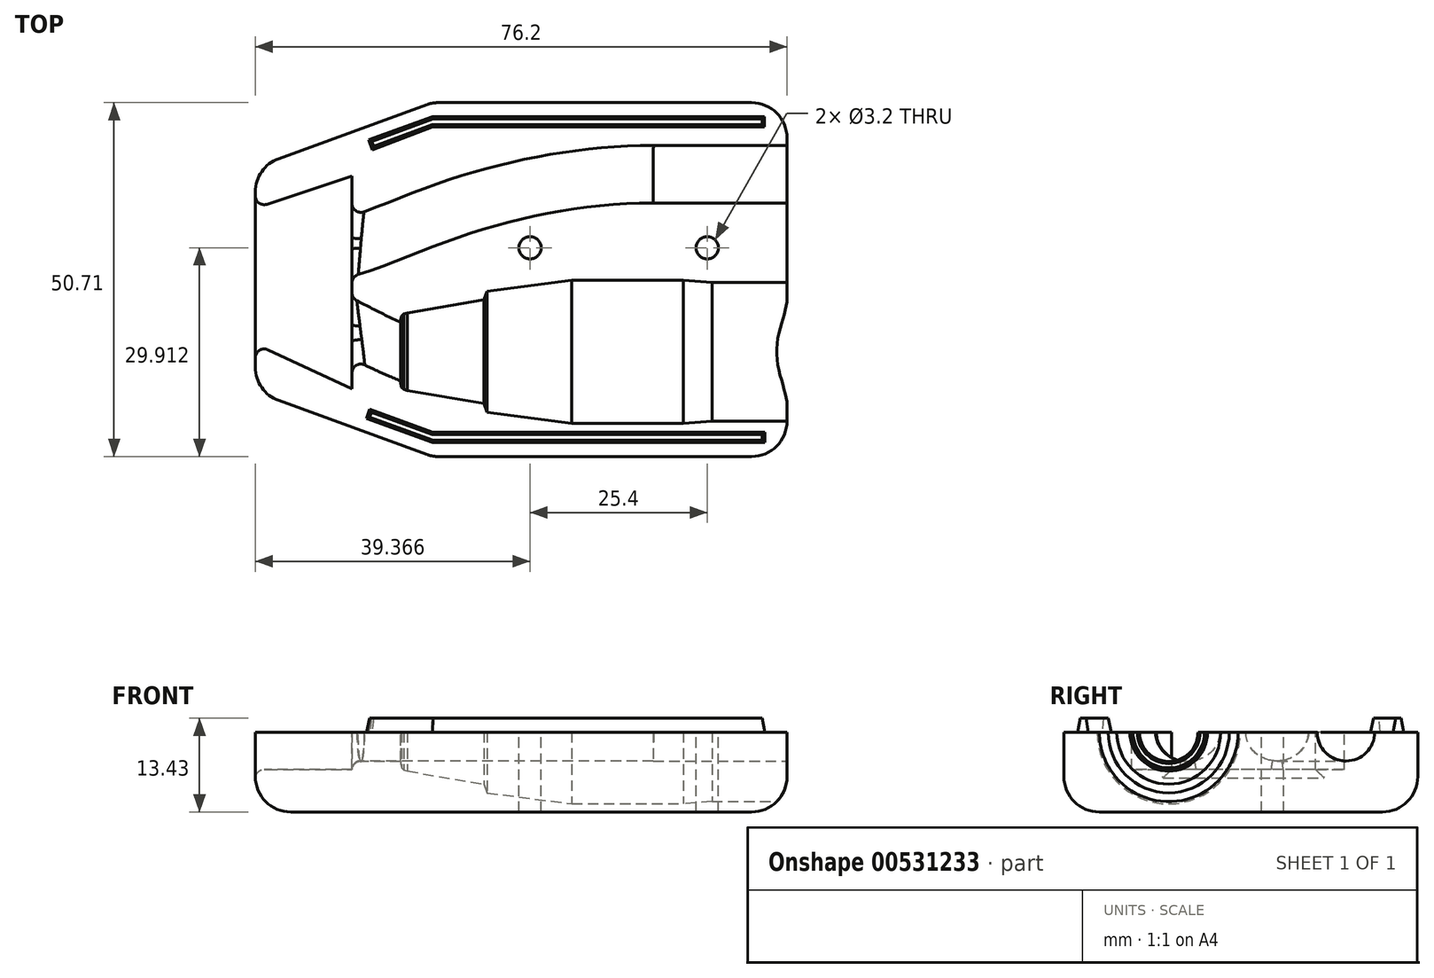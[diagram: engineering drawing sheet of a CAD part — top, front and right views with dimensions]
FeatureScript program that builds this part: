
annotation { "Feature Type Name" : "Feature", "Feature Type Description" : "" }
export const myFeature = defineFeature(function(context is Context, id is Id, definition is map)
    precondition{}
    {
        {
            var Q0;
            Q0=qCreatedBy(makeId("Top.planeOp"),FACE);
            var sketch = newSketch(context, id + "F0", { "sketchPlane" : qUnion([Q0])});
            skLineSegment(sketch, "E0", {"start": v(-28.61, 2.44) * mm, "end": v(45.8, 2.44) * mm});
            skLineSegment(sketch, "E1", {"start": v(45.8, 2.44) * mm, "end": v(45.8, -7.5) * mm});
            skLineSegment(sketch, "E2", {"start": v(45.8, -7.5) * mm, "end": v(33.92, -7.5) * mm});
            skLineSegment(sketch, "E3", {"start": v(33.92, -7.5) * mm, "end": v(31.07, -7.5) * mm});
            skLineSegment(sketch, "E4", {"start": v(31.07, -7.5) * mm, "end": v(15.98, -7.5) * mm});
            skLineSegment(sketch, "E5", {"start": v(15.98, -7.5) * mm, "end": v(11.85, -7.82) * mm});
            skLineSegment(sketch, "E6", {"start": v(11.85, -7.82) * mm, "end": v(-4.1, -7.82) * mm});
            skLineSegment(sketch, "E7", {"start": v(-4.1, -7.82) * mm, "end": v(-16.21, -6.24) * mm});
            skLineSegment(sketch, "E8", {"start": v(-16.21, -6.24) * mm, "end": v(-16.67, -5) * mm});
            skLineSegment(sketch, "E9", {"start": v(-16.67, -5) * mm, "end": v(-27.65, -3.12) * mm});
            skLineSegment(sketch, "E10", {"start": v(-27.65, -3.12) * mm, "end": v(-28.19, -2.96) * mm});
            skLineSegment(sketch, "E11", {"start": v(-28.19, -2.96) * mm, "end": v(-28.49, -2.68) * mm});
            skLineSegment(sketch, "E12", {"start": v(-28.49, -2.68) * mm, "end": v(-28.63, -2.06) * mm});
            skLineSegment(sketch, "E13", {"start": v(-28.63, -2.06) * mm, "end": v(-28.61, 2.44) * mm});
            skLineSegment(sketch, "E14.top", {"start": v(32.8, 22.64) * mm, "end": v(45.8, 22.64) * mm});
            skLineSegment(sketch, "E14.right", {"start": v(45.8, 27.84) * mm, "end": v(45.8, 22.64) * mm});
            skLineSegment(sketch, "E15", {"start": v(32.8, 23.72) * mm, "end": v(24.8, 23.72) * mm});
            skLineSegment(sketch, "E16", {"start": v(24.8, 23.72) * mm, "end": v(24.8, 27.84) * mm});
            skLineSegment(sketch, "E17", {"start": v(45.8, 27.84) * mm, "end": v(24.8, 27.84) * mm});
            skLineSegment(sketch, "E18", {"start": v(32.8, 22.64) * mm, "end": v(32.8, 23.72) * mm});
            skLineSegment(sketch, "E19.MirrorCS", {"start": v(32.8, 33.05) * mm, "end": v(32.8, 31.97) * mm});
            skLineSegment(sketch, "E20.MirrorCS", {"start": v(32.8, 33.05) * mm, "end": v(45.8, 33.05) * mm});
            skLineSegment(sketch, "E21.MirrorCS", {"start": v(45.8, 27.84) * mm, "end": v(45.8, 33.05) * mm});
            skLineSegment(sketch, "E22.MirrorCS", {"start": v(24.8, 31.97) * mm, "end": v(24.8, 27.84) * mm});
            skLineSegment(sketch, "E23.MirrorCS", {"start": v(32.8, 31.97) * mm, "end": v(24.8, 31.97) * mm});
            skLineSegment(sketch, "E24.MirrorCS", {"start": v(-28.19, 7.85) * mm, "end": v(-28.49, 7.56) * mm});
            skLineSegment(sketch, "E25.MirrorCS", {"start": v(-28.49, 7.56) * mm, "end": v(-28.63, 6.94) * mm});
            skLineSegment(sketch, "E26.MirrorCS", {"start": v(33.92, 12.39) * mm, "end": v(31.07, 12.39) * mm});
            skLineSegment(sketch, "E27.MirrorCS", {"start": v(-27.65, 8) * mm, "end": v(-28.19, 7.85) * mm});
            skLineSegment(sketch, "E28.MirrorCS", {"start": v(-16.21, 11.12) * mm, "end": v(-16.67, 9.89) * mm});
            skLineSegment(sketch, "E29.MirrorCS", {"start": v(-16.67, 9.89) * mm, "end": v(-27.65, 8) * mm});
            skLineSegment(sketch, "E30.MirrorCS", {"start": v(11.85, 12.7) * mm, "end": v(-4.1, 12.7) * mm});
            skLineSegment(sketch, "E31.MirrorCS", {"start": v(45.8, 12.39) * mm, "end": v(33.92, 12.39) * mm});
            skLineSegment(sketch, "E32.MirrorCS", {"start": v(-4.1, 12.7) * mm, "end": v(-16.21, 11.12) * mm});
            skLineSegment(sketch, "E33.MirrorCS", {"start": v(15.98, 12.39) * mm, "end": v(11.85, 12.7) * mm});
            skLineSegment(sketch, "E34.MirrorCS", {"start": v(31.07, 12.39) * mm, "end": v(15.98, 12.39) * mm});
            skLineSegment(sketch, "E35.MirrorCS", {"start": v(45.8, 2.44) * mm, "end": v(45.8, 12.39) * mm});
            skLineSegment(sketch, "E36.MirrorCS", {"start": v(-28.63, 6.94) * mm, "end": v(-28.61, 2.44) * mm});
            skSolve(sketch);
        }
        {
            var Q0;
            Q0=qCreatedBy(makeId("Top.planeOp"),FACE);
            var sketch = newSketch(context, id + "F1", { "sketchPlane" : qUnion([Q0])});
            skLineSegment(sketch, "E37.0", {"start": v(45.8, 2.44) * mm, "end": v(45.8, -7.5) * mm});
            skLineSegment(sketch, "E38.0", {"start": v(45.8, 27.84) * mm, "end": v(45.8, 22.64) * mm});
            skLineSegment(sketch, "E39", {"start": v(26.75, 38.13) * mm, "end": v(26.75, -12.58) * mm});
            skLineSegment(sketch, "E40", {"start": v(26.75, -12.58) * mm, "end": v(-24.05, -12.58) * mm});
            skLineSegment(sketch, "E41", {"start": v(-24.05, -12.58) * mm, "end": v(-49.45, -3.34) * mm});
            skLineSegment(sketch, "E42", {"start": v(-49.45, -3.34) * mm, "end": v(-49.45, 28.88) * mm});
            skLineSegment(sketch, "E43", {"start": v(-49.45, 28.88) * mm, "end": v(-24.05, 38.13) * mm});
            skLineSegment(sketch, "E44", {"start": v(-24.05, 38.13) * mm, "end": v(26.75, 38.13) * mm});
            skLineSegment(sketch, "E45.0", {"start": v(45.8, 27.84) * mm, "end": v(45.8, 33.05) * mm});
            skSolve(sketch);
        }
        {
            var Q0;
            Q0 = qSketchRegion(id + "F1", true);
            extrude(context, id + "F2", {"entities" : qUnion([Q0]), "oppositeDirection" : true, "depth" : 11.43 * mm, "offsetDistance" : 25.4 * mm});
        }
        {
            var Q0;
            Q0=makeQuery(id+"F0.imprint","IMPRINT",FACE,{"disambiguationData":[TD([[makeQuery(id+"F0.imprint","IMPRINT",EDGE,{"derivedFrom":sQuery(id+"F0.wireOp",EDGE,"E0")}),-1.0]])]});
            var Q1;
            Q1=sQuery(id+"F0.wireOp",EDGE,"E0");
            revolve(context, id + "F3", {"operationType" : NewBodyOperationType.REMOVE, "entities" : qUnion([Q0]), "axis" : qUnion([Q1]), "revolveType" : RevolveType.FULL, "oppositeDirection" : true});
        }
        {
            var Q0;
            Q0=makeQuery(id+"F0.imprint","IMPRINT",FACE,{"disambiguationData":[TD([[makeQuery(id+"F0.imprint","IMPRINT",EDGE,{"derivedFrom":sQuery(id+"F0.wireOp",EDGE,"E14.top")}),1.0]])]});
            var Q1;
            Q1=sQuery(id+"F0.wireOp",EDGE,"E17");
            revolve(context, id + "F4", {"operationType" : NewBodyOperationType.REMOVE, "entities" : qUnion([Q0]), "axis" : qUnion([Q1]), "revolveType" : RevolveType.FULL});
        }
        {
            var Q0;
            Q0=makeQuery(id+"F2.opExtrude","CAP_FACE",FACE,{"disambiguationData":[OSD([sQuery(id+"F1.wireOp",EDGE,"FN9DgEXL-DUnT-EqR8-ggIH-wTex11pTKOJ6"),sQuery(id+"F1.wireOp",EDGE,"Mmaicck8-LA38-ALDy-QV3c-pMFCgAv4KP83"),sQuery(id+"F1.wireOp",EDGE,"E39"),sQuery(id+"F1.wireOp",EDGE,"E40"),sQuery(id+"F1.wireOp",EDGE,"E41"),sQuery(id+"F1.wireOp",EDGE,"E42"),sQuery(id+"F1.wireOp",EDGE,"E43"),sQuery(id+"F1.wireOp",EDGE,"E44")])],"isStart":true});
            var sketch = newSketch(context, id + "F5", { "sketchPlane" : qUnion([Q0])});
            skLineSegment(sketch, "E46.0", {"start": v(-28.61, 2.44) * mm, "end": v(45.8, 2.44) * mm});
            skFitSpline(sketch, "E47", {"points": [v(-28.61, 2.44) * mm, v(-48.07, 10.49) * mm, v(-83.77, 9.93) * mm], "startDerivative": vector(-48.46, 20.5) * mm, "endDerivative": vector(-77.25, 2.74) * mm});
            skSolve(sketch);
        }
        {
            var Q0;
            Q0=sQuery(id+"F5.wireOp",VERTEX,"E47.0.internal");
            var Q1;
            Q1=sQuery(id+"F5.wireOp",EDGE,"E46.0");
            cPlane(context, id + "F6", {"entities" : qUnion([Q0, Q1]), "cplaneType" : CPlaneType.LINE_POINT, "offset" : 25.4 * mm, "width" : 152.4 * mm, "height" : 152.4 * mm});
        }
        {
            var Q0;
            Q0=qCreatedBy(id+"F6.planeOp",FACE);
            var sketch = newSketch(context, id + "F7", { "sketchPlane" : qUnion([Q0])});
            skCircle(sketch, "E48", {"center": v(2.44, 0) * mm, "radius": 4.2 * mm});
            skSolve(sketch);
        }
        {
            var Q0;
            Q0 = qSketchRegion(id + "F7", true);
            var Q1;
            Q1=sQuery(id+"F5.wireOp",EDGE,"E47");
            sweep(context, id + "F8", {"operationType" : NewBodyOperationType.REMOVE, "profiles" : qUnion([Q0]), "path" : qUnion([Q1])});
        }
        {
            var Q0;
            Q0=sQuery(id+"F0.wireOp",VERTEX,"E22.MirrorCS.end");
            var Q1;
            Q1=sQuery(id+"F0.wireOp",EDGE,"E17");
            cPlane(context, id + "F9", {"entities" : qUnion([Q0, Q1]), "cplaneType" : CPlaneType.LINE_POINT, "offset" : 25.4 * mm, "width" : 152.4 * mm, "height" : 152.4 * mm});
        }
        {
            var Q0;
            {var subQ0=sQuery(id+"F1.wireOp",EDGE,"E39");var subQ1=sQuery(id+"F1.wireOp",EDGE,"E42");var subQ2=sQuery(id+"F1.wireOp",EDGE,"E43");var subQ3=sQuery(id+"F1.wireOp",EDGE,"E44");Q0=makeQuery(id+"F8.boolean.opBoolean","SPLIT",FACE,{"disambiguationData":[TD([makeQuery(id+"F2.opExtrude","SWEPT_FACE",FACE,{"disambiguationData":[OSD([subQ2])]})])],"derivedFrom":makeQuery(id+"F2.opExtrude","CAP_FACE",FACE,{"disambiguationData":[OSD([subQ0,sQuery(id+"F1.wireOp",EDGE,"E40"),sQuery(id+"F1.wireOp",EDGE,"E41"),subQ1,subQ2,subQ3])],"isStart":true})});}
            var sketch = newSketch(context, id + "F10", { "sketchPlane" : qUnion([Q0])});
            skLineSegment(sketch, "E49", {"start": v(24.8, 27.84) * mm, "end": v(7.57, 27.84) * mm});
            skFitSpline(sketch, "E50", {"points": [v(7.57, 27.84) * mm, v(-20.4, 23.18) * mm, v(-39.19, 16.58) * mm, v(-88.02, 16.43) * mm], "startDerivative": vector(-85.25, 1.29) * mm, "endDerivative": vector(-186.21, 7.59) * mm});
            skSolve(sketch);
        }
        {
            var Q0;
            Q0=qCreatedBy(id+"F9.planeOp",FACE);
            var sketch = newSketch(context, id + "F11", { "sketchPlane" : qUnion([Q0])});
            skCircle(sketch, "E51", {"center": v(-27.84, 0) * mm, "radius": 4.12 * mm});
            skSolve(sketch);
        }
        {
            var Q0;
            Q0 = qSketchRegion(id + "F11", true);
            var Q1;
            Q1=sQuery(id+"F10.wireOp",EDGE,"E49");
            var Q2;
            Q2=sQuery(id+"F10.wireOp",EDGE,"E50");
            sweep(context, id + "F12", {"operationType" : NewBodyOperationType.REMOVE, "profiles" : qUnion([Q0]), "path" : qUnion([Q1, Q2])});
        }
        {
            var Q0;
            {var subQ3=sQuery(id+"F1.wireOp",EDGE,"E39");var subQ8=sQuery(id+"F1.wireOp",EDGE,"E42");var subQ10=makeQuery(id+"F3.boolean.opBoolean","COPY",FACE,{"derivedFrom":makeQuery(id+"F3.opRevolve","SWEPT_FACE",FACE,{"disambiguationData":[OSD([sQuery(id+"F0.wireOp",EDGE,"E4")])]})});var subQ17=sQuery(id+"F1.wireOp",EDGE,"E43");var subQ18=sQuery(id+"F1.wireOp",EDGE,"E44");Q0=makeQuery(id+"F12.boolean.opBoolean","SPLIT",FACE,{"disambiguationData":[TD([subQ10])],"derivedFrom":makeQuery(id+"F8.boolean.opBoolean","SPLIT",FACE,{"disambiguationData":[TD([makeQuery(id+"F2.opExtrude","SWEPT_FACE",FACE,{"disambiguationData":[OSD([subQ17])]})])],"derivedFrom":makeQuery(id+"F2.opExtrude","CAP_FACE",FACE,{"disambiguationData":[OSD([subQ3,sQuery(id+"F1.wireOp",EDGE,"E40"),sQuery(id+"F1.wireOp",EDGE,"E41"),subQ8,subQ17,subQ18])],"isStart":true})})});}
            var sketch = newSketch(context, id + "F13", { "sketchPlane" : qUnion([Q0])});
            skLineSegment(sketch, "E52", {"start": v(-49.97, 22.84) * mm, "end": v(-35.6, 27.6) * mm});
            skLineSegment(sketch, "E53", {"start": v(-35.6, 27.6) * mm, "end": v(-35.6, -2.85) * mm});
            skLineSegment(sketch, "E54", {"start": v(-35.6, -2.85) * mm, "end": v(-49.98, 3.8) * mm});
            skLineSegment(sketch, "E55", {"start": v(-49.97, 22.84) * mm, "end": v(-49.98, 3.8) * mm});
            skSolve(sketch);
        }
        {
            var Q0;
            Q0 = qSketchRegion(id + "F13", true);
            extrude(context, id + "F14", {"entities" : qUnion([Q0]), "operationType" : NewBodyOperationType.REMOVE, "oppositeDirection" : true, "depth" : 5.33 * mm, "offsetDistance" : 25.4 * mm});
        }
        {
            var Q0;
            {var subQ3=sQuery(id+"F1.wireOp",EDGE,"E39");var subQ8=sQuery(id+"F1.wireOp",EDGE,"E42");var subQ10=makeQuery(id+"F3.boolean.opBoolean","COPY",FACE,{"derivedFrom":makeQuery(id+"F3.opRevolve","SWEPT_FACE",FACE,{"disambiguationData":[OSD([sQuery(id+"F0.wireOp",EDGE,"E4")])]})});var subQ17=sQuery(id+"F1.wireOp",EDGE,"E43");var subQ18=sQuery(id+"F1.wireOp",EDGE,"E44");Q0=makeQuery(id+"F12.boolean.opBoolean","SPLIT",FACE,{"disambiguationData":[TD([subQ10])],"derivedFrom":makeQuery(id+"F8.boolean.opBoolean","SPLIT",FACE,{"disambiguationData":[TD([makeQuery(id+"F2.opExtrude","SWEPT_FACE",FACE,{"disambiguationData":[OSD([subQ17])]})])],"derivedFrom":makeQuery(id+"F2.opExtrude","CAP_FACE",FACE,{"disambiguationData":[OSD([subQ3,sQuery(id+"F1.wireOp",EDGE,"E40"),sQuery(id+"F1.wireOp",EDGE,"E41"),subQ8,subQ17,subQ18])],"isStart":true})})});}
            var sketch = newSketch(context, id + "F15", { "sketchPlane" : qUnion([Q0])});
            skCircle(sketch, "E56", {"center": v(-10.08, 17.33) * mm, "radius": 1.6 * mm});
            skCircle(sketch, "E57", {"center": v(15.32, 17.33) * mm, "radius": 1.6 * mm});
            skLineSegment(sketch, "E58.0", {"start": v(-24.05, 38.13) * mm, "end": v(26.75, 38.13) * mm});
            skLineSegment(sketch, "E59.0", {"start": v(26.75, -12.58) * mm, "end": v(-24.05, -12.58) * mm});
            skLineSegment(sketch, "E60.0", {"start": v(-49.45, 28.88) * mm, "end": v(-24.05, 38.13) * mm});
            skLineSegment(sketch, "E61.0", {"start": v(-24.05, -12.58) * mm, "end": v(-49.45, -3.34) * mm});
            skSolve(sketch);
        }
        {
            var Q0;
            Q0 = qSketchRegion(id + "F15", true);
            extrude(context, id + "F16", {"entities" : qUnion([Q0]), "operationType" : NewBodyOperationType.REMOVE, "oppositeDirection" : true, "depth" : 25.4 * mm, "offsetDistance" : 25.4 * mm});
        }
        {
            var Q0;
            {var subQ3=sQuery(id+"F1.wireOp",EDGE,"E39");var subQ8=sQuery(id+"F1.wireOp",EDGE,"E42");var subQ10=makeQuery(id+"F3.boolean.opBoolean","COPY",FACE,{"derivedFrom":makeQuery(id+"F3.opRevolve","SWEPT_FACE",FACE,{"disambiguationData":[OSD([sQuery(id+"F0.wireOp",EDGE,"E4")])]})});var subQ17=sQuery(id+"F1.wireOp",EDGE,"E43");var subQ18=sQuery(id+"F1.wireOp",EDGE,"E44");Q0=makeQuery(id+"F12.boolean.opBoolean","SPLIT",FACE,{"disambiguationData":[TD([subQ10])],"derivedFrom":makeQuery(id+"F8.boolean.opBoolean","SPLIT",FACE,{"disambiguationData":[TD([makeQuery(id+"F2.opExtrude","SWEPT_FACE",FACE,{"disambiguationData":[OSD([subQ17])]})])],"derivedFrom":makeQuery(id+"F2.opExtrude","CAP_FACE",FACE,{"disambiguationData":[OSD([subQ3,sQuery(id+"F1.wireOp",EDGE,"E40"),sQuery(id+"F1.wireOp",EDGE,"E41"),subQ8,subQ17,subQ18])],"isStart":true})})});}
            var sketch = newSketch(context, id + "F17", { "sketchPlane" : qUnion([Q0])});
            skLineSegment(sketch, "E62.0", {"start": v(-49.45, 28.88) * mm, "end": v(-24.05, 38.13) * mm});
            skLineSegment(sketch, "E63.0", {"start": v(-24.05, 38.13) * mm, "end": v(26.75, 38.13) * mm});
            skLineSegment(sketch, "E64.0", {"start": v(-24.05, -12.58) * mm, "end": v(-49.45, -3.34) * mm});
            skLineSegment(sketch, "E65.1", {"start": v(26.75, -12.58) * mm, "end": v(-24.05, -12.58) * mm});
            skLineSegment(sketch, "E66", {"start": v(-33.23, 32.8) * mm, "end": v(-24.05, 36.13) * mm});
            skLineSegment(sketch, "E67", {"start": v(-24.05, 36.13) * mm, "end": v(23.52, 36.13) * mm});
            skLineSegment(sketch, "E68", {"start": v(23.52, 36.13) * mm, "end": v(23.52, 34.63) * mm});
            skLineSegment(sketch, "E69", {"start": v(23.52, 34.63) * mm, "end": v(-24.05, 34.63) * mm});
            skLineSegment(sketch, "E70", {"start": v(-33.23, 32.8) * mm, "end": v(-32.72, 31.38) * mm});
            skLineSegment(sketch, "E71", {"start": v(-32.72, 31.38) * mm, "end": v(-24.05, 34.63) * mm});
            skLineSegment(sketch, "E72", {"start": v(-33.53, -7.13) * mm, "end": v(-24.05, -10.58) * mm});
            skLineSegment(sketch, "E73", {"start": v(-24.05, -10.58) * mm, "end": v(23.57, -10.58) * mm});
            skLineSegment(sketch, "E74", {"start": v(23.57, -10.58) * mm, "end": v(23.57, -9.08) * mm});
            skLineSegment(sketch, "E75", {"start": v(23.57, -9.08) * mm, "end": v(-24.05, -9.08) * mm});
            skLineSegment(sketch, "E76", {"start": v(-24.05, -9.08) * mm, "end": v(-33.05, -5.8) * mm});
            skLineSegment(sketch, "E77", {"start": v(-33.05, -5.8) * mm, "end": v(-33.53, -7.13) * mm});
            skSolve(sketch);
        }
        {
            var Q0;
            Q0 = qSketchRegion(id + "F17", true);
            extrude(context, id + "F18", {"entities" : qUnion([Q0]), "operationType" : NewBodyOperationType.ADD, "depth" : 2 * mm, "offsetDistance" : 25.4 * mm, "hasDraft" : true, "draftAngle" : 10 * degree, "draftPullDirection" : true});
        }
        {
            var Q0;
            Q0=makeQuery(id+"F14.boolean.opBoolean","INTERSECT",EDGE,{"derivedFrom":[makeQuery(id+"F2.opExtrude","SWEPT_FACE",FACE,{"disambiguationData":[OSD([sQuery(id+"F1.wireOp",EDGE,"E42")])]}),makeQuery(id+"F14.opExtrude","SWEPT_FACE",FACE,{"disambiguationData":[OSD([sQuery(id+"F13.wireOp",EDGE,"E52")])]})]});
            var Q1;
            Q1=makeQuery(id+"F14.boolean.opBoolean","INTERSECT",EDGE,{"derivedFrom":[makeQuery(id+"F2.opExtrude","SWEPT_FACE",FACE,{"disambiguationData":[OSD([sQuery(id+"F1.wireOp",EDGE,"E42")])]}),makeQuery(id+"F14.opExtrude","SWEPT_FACE",FACE,{"disambiguationData":[OSD([sQuery(id+"F13.wireOp",EDGE,"E54")])]})]});
            var Q2;
            Q2=makeQuery(id+"F14.boolean.opBoolean","INTERSECT",EDGE,{"derivedFrom":[makeQuery(id+"F2.opExtrude","SWEPT_FACE",FACE,{"disambiguationData":[OSD([sQuery(id+"F1.wireOp",EDGE,"E42")])]}),makeQuery(id+"F14.opExtrude","CAP_FACE",FACE,{"disambiguationData":[OSD([sQuery(id+"F13.wireOp",EDGE,"E52"),sQuery(id+"F13.wireOp",EDGE,"E53"),sQuery(id+"F13.wireOp",EDGE,"E54"),sQuery(id+"F13.wireOp",EDGE,"E55")])],"isStart":false})]});
            fillet(context, id + "F19", {"entities" : qUnion([Q0, Q1, Q2]), "radius" : 1.27 * mm, "tangentPropagation" : true, "allowEdgeOverflow" : false});
        }
        {
            var Q0;
            Q0=makeQuery(id+"F14.boolean.opBoolean","INTERSECT",EDGE,{"derivedFrom":[makeQuery(id+"F12.boolean.opBoolean","COPY",FACE,{"derivedFrom":makeQuery(id+"F12.opSweep","SWEPT_FACE",FACE,{"disambiguationData":[OSD([sQuery(id+"F10.wireOp",EDGE,"E50"),sQuery(id+"F11.wireOp",EDGE,"E51")])]})}),makeQuery(id+"F14.opExtrude","SWEPT_FACE",FACE,{"disambiguationData":[OSD([sQuery(id+"F13.wireOp",EDGE,"E53")])]})]});
            var Q1;
            Q1=makeQuery(id+"F14.boolean.opBoolean","INTERSECT",EDGE,{"derivedFrom":[makeQuery(id+"F8.boolean.opBoolean","COPY",FACE,{"derivedFrom":makeQuery(id+"F8.opSweep","SWEPT_FACE",FACE,{"disambiguationData":[OSD([sQuery(id+"F5.wireOp",EDGE,"E47"),sQuery(id+"F7.wireOp",EDGE,"E48")])]})}),makeQuery(id+"F14.opExtrude","SWEPT_FACE",FACE,{"disambiguationData":[OSD([sQuery(id+"F13.wireOp",EDGE,"E53")])]})]});
            fillet(context, id + "F20", {"entities" : qUnion([Q0, Q1]), "radius" : 1.27 * mm, "tangentPropagation" : true, "allowEdgeOverflow" : false});
        }
        {
            var Q0;
            Q0=makeQuery(id+"F2.opExtrude","CAP_EDGE",EDGE,{"disambiguationData":[OSD([sQuery(id+"F1.wireOp",EDGE,"E40")])],"isStart":false});
            var Q1;
            Q1=makeQuery(id+"F2.opExtrude","CAP_EDGE",EDGE,{"disambiguationData":[OSD([sQuery(id+"F1.wireOp",EDGE,"E41")])],"isStart":false});
            var Q2;
            Q2=makeQuery(id+"F2.opExtrude","SWEPT_EDGE",EDGE,{"disambiguationData":[OSD([sQuery(id+"F1.wireOp",EDGE,"E40"),sQuery(id+"F1.wireOp",EDGE,"E41")])]});
            var Q3;
            Q3=makeQuery(id+"F2.opExtrude","SWEPT_EDGE",EDGE,{"disambiguationData":[OSD([sQuery(id+"F1.wireOp",EDGE,"E41"),sQuery(id+"F1.wireOp",EDGE,"E42")])]});
            var Q4;
            Q4=makeQuery(id+"F2.opExtrude","SWEPT_EDGE",EDGE,{"disambiguationData":[OSD([sQuery(id+"F1.wireOp",EDGE,"E39"),sQuery(id+"F1.wireOp",EDGE,"E40")])]});
            var Q5;
            Q5=makeQuery(id+"F2.opExtrude","CAP_EDGE",EDGE,{"disambiguationData":[OSD([sQuery(id+"F1.wireOp",EDGE,"E39")])],"isStart":false});
            var Q6;
            Q6=makeQuery(id+"F2.opExtrude","SWEPT_EDGE",EDGE,{"disambiguationData":[OSD([sQuery(id+"F1.wireOp",EDGE,"E39"),sQuery(id+"F1.wireOp",EDGE,"E44")])]});
            var Q7;
            Q7=makeQuery(id+"F2.opExtrude","CAP_EDGE",EDGE,{"disambiguationData":[OSD([sQuery(id+"F1.wireOp",EDGE,"E44")])],"isStart":false});
            var Q8;
            Q8=makeQuery(id+"F2.opExtrude","SWEPT_EDGE",EDGE,{"disambiguationData":[OSD([sQuery(id+"F1.wireOp",EDGE,"E43"),sQuery(id+"F1.wireOp",EDGE,"E44")])]});
            var Q9;
            Q9=makeQuery(id+"F2.opExtrude","CAP_EDGE",EDGE,{"disambiguationData":[OSD([sQuery(id+"F1.wireOp",EDGE,"E43")])],"isStart":false});
            var Q10;
            Q10=makeQuery(id+"F2.opExtrude","SWEPT_EDGE",EDGE,{"disambiguationData":[OSD([sQuery(id+"F1.wireOp",EDGE,"E42"),sQuery(id+"F1.wireOp",EDGE,"E43")])]});
            var Q11;
            Q11=makeQuery(id+"F2.opExtrude","CAP_EDGE",EDGE,{"disambiguationData":[OSD([sQuery(id+"F1.wireOp",EDGE,"E42")])],"isStart":false});
            fillet(context, id + "F21", {"entities" : qUnion([Q0, Q1, Q2, Q3, Q4, Q5, Q6, Q7, Q8, Q9, Q10, Q11]), "radius" : 5.08 * mm, "tangentPropagation" : true, "allowEdgeOverflow" : false});
        }
    });
